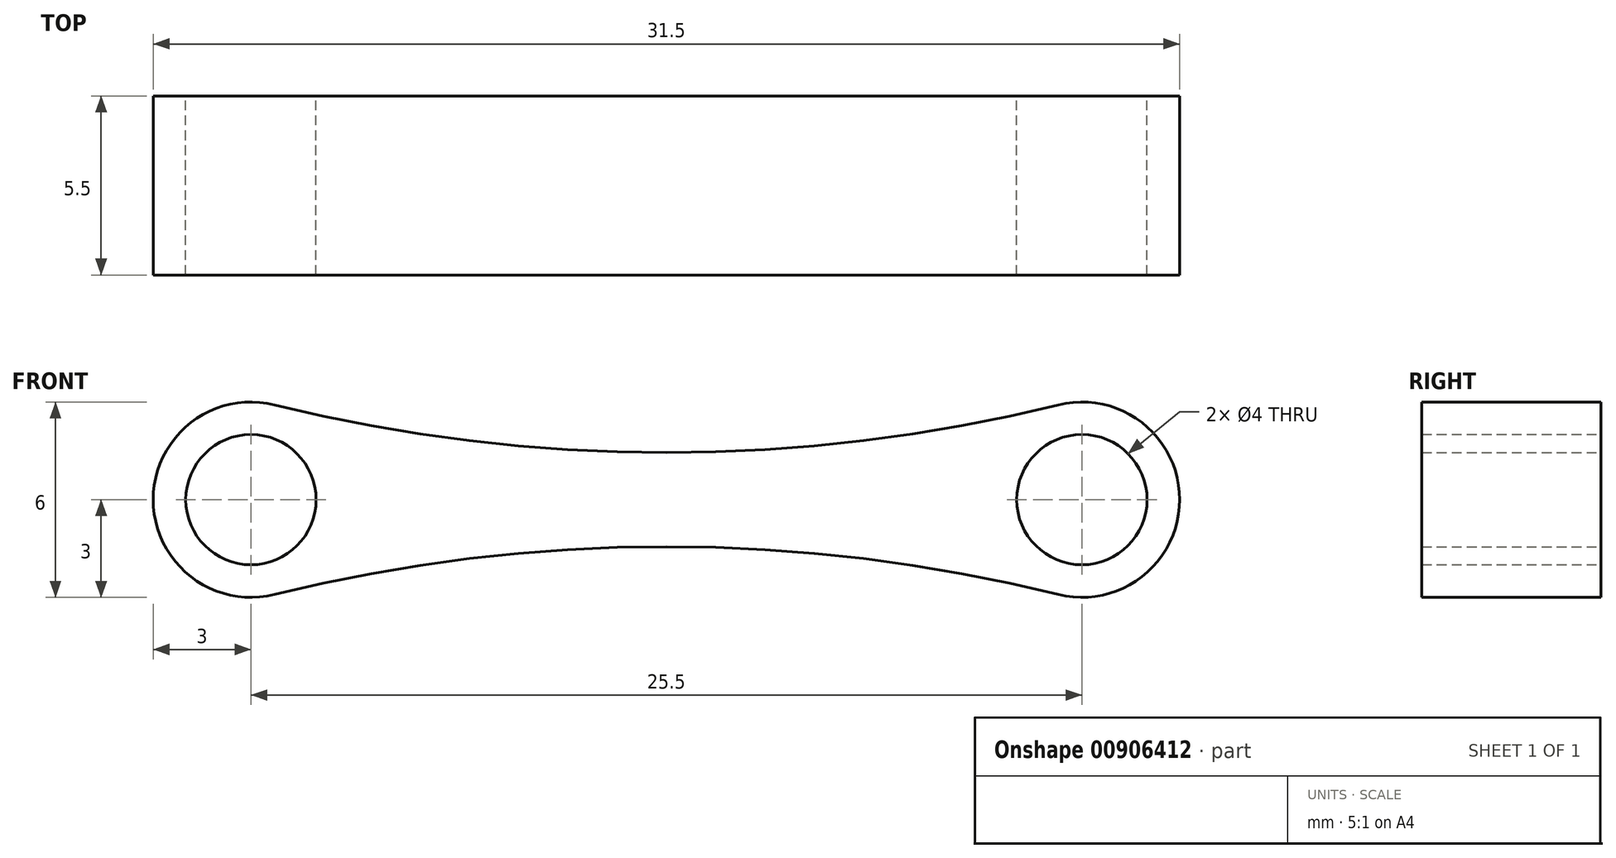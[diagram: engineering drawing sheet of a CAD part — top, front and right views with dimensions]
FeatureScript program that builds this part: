
annotation { "Feature Type Name" : "Feature", "Feature Type Description" : "" }
export const myFeature = defineFeature(function(context is Context, id is Id, definition is map)
    precondition{}
    {
        {
            var Q0;
            Q0=qCreatedBy(makeId("Front.planeOp"),FACE);
            var sketch = newSketch(context, id + "F0", { "sketchPlane" : qUnion([Q0])});
            skLineSegment(sketch, "E0", {"start": v(-12.75, 0) * mm, "end": v(12.75, 0) * mm, "construction": true});
            skCircle(sketch, "E1", {"center": v(12.75, 0) * mm, "radius": 2 * mm});
            skArc(sketch, "E2", {"start": v(12.03, -2.91) * mm, "mid": v(15.75, 0) * mm, "end": v(12.03, 2.91) * mm});
            skCircle(sketch, "E3", {"center": v(-12.75, 0) * mm, "radius": 2 * mm});
            skArc(sketch, "E4", {"start": v(-12.03, 2.91) * mm, "mid": v(-15.75, 0) * mm, "end": v(-12.03, -2.91) * mm});
            skArc(sketch, "E5", {"start": v(12.03, -2.91) * mm, "mid": v(0, -1.44) * mm, "end": v(-12.03, -2.91) * mm});
            skArc(sketch, "E6.MirrorCS", {"start": v(12.03, 2.91) * mm, "mid": v(0, 1.44) * mm, "end": v(-12.03, 2.91) * mm});
            skSolve(sketch);
        }
        {
            var Q0;
            Q0=makeQuery(id+"F0.imprint","IMPRINT",FACE,{"disambiguationData":[TD([[makeQuery(id+"F0.imprint","IMPRINT",EDGE,{"derivedFrom":sQuery(id+"F0.wireOp",EDGE,"E1")}),-1.0]])]});
            extrude(context, id + "F1", {"entities" : qUnion([Q0]), "depth" : 5.5 * mm, "offsetDistance" : 25 * mm});
        }
    });
